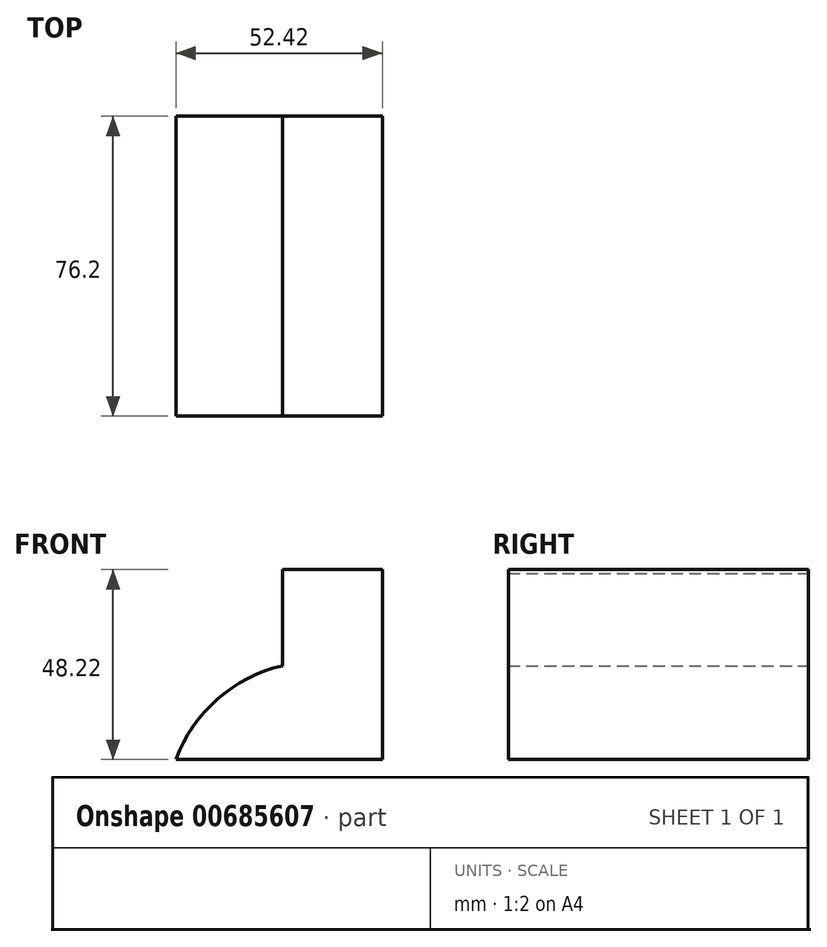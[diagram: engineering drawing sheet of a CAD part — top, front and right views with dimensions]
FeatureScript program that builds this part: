
annotation { "Feature Type Name" : "Feature", "Feature Type Description" : "" }
export const myFeature = defineFeature(function(context is Context, id is Id, definition is map)
    precondition{}
    {
        {
            var Q0;
            Q0=qCreatedBy(makeId("Front.planeOp"),FACE);
            var sketch = newSketch(context, id + "F0", { "sketchPlane" : qUnion([Q0])});
            skLineSegment(sketch, "E0", {"start": v(0, 48.22) * mm, "end": v(0, 0) * mm});
            skLineSegment(sketch, "E1", {"start": v(0, 0) * mm, "end": v(-52.42, 0) * mm});
            skArc(sketch, "E2", {"start": v(-25.3, 23.77) * mm, "mid": v(-41.86, 15.31) * mm, "end": v(-52.42, 0) * mm});
            skLineSegment(sketch, "E3", {"start": v(-25.3, 23.77) * mm, "end": v(-25.3, 47.26) * mm});
            skLineSegment(sketch, "E4", {"start": v(-25.3, 47.26) * mm, "end": v(0, 48.22) * mm});
            skLineSegment(sketch, "E5", {"start": v(-25.3, 47.26) * mm, "end": v(-25.34, 48.22) * mm});
            skLineSegment(sketch, "E6", {"start": v(-25.34, 48.22) * mm, "end": v(0, 48.22) * mm});
            skSolve(sketch);
        }
        {
            var Q0;
            Q0 = qSketchRegion(id + "F0", true);
            extrude(context, id + "F1", {"entities" : qUnion([Q0]), "depth" : 25.4 * mm, "offsetDistance" : 25.4 * mm});
        }
        {
            var Q0;
            Q0=makeQuery(id+"F1.opExtrude","CAP_FACE",FACE,{"disambiguationData":[OSD([sQuery(id+"F0.wireOp",EDGE,"E0"),sQuery(id+"F0.wireOp",EDGE,"E1"),sQuery(id+"F0.wireOp",EDGE,"E2"),sQuery(id+"F0.wireOp",EDGE,"E3"),sQuery(id+"F0.wireOp",EDGE,"E5"),sQuery(id+"F0.wireOp",EDGE,"E6")])],"isStart":false});
            extrude(context, id + "F2", {"entities" : qUnion([Q0]), "operationType" : NewBodyOperationType.ADD, "depth" : 50.8 * mm, "offsetDistance" : 25.4 * mm});
        }
    });
